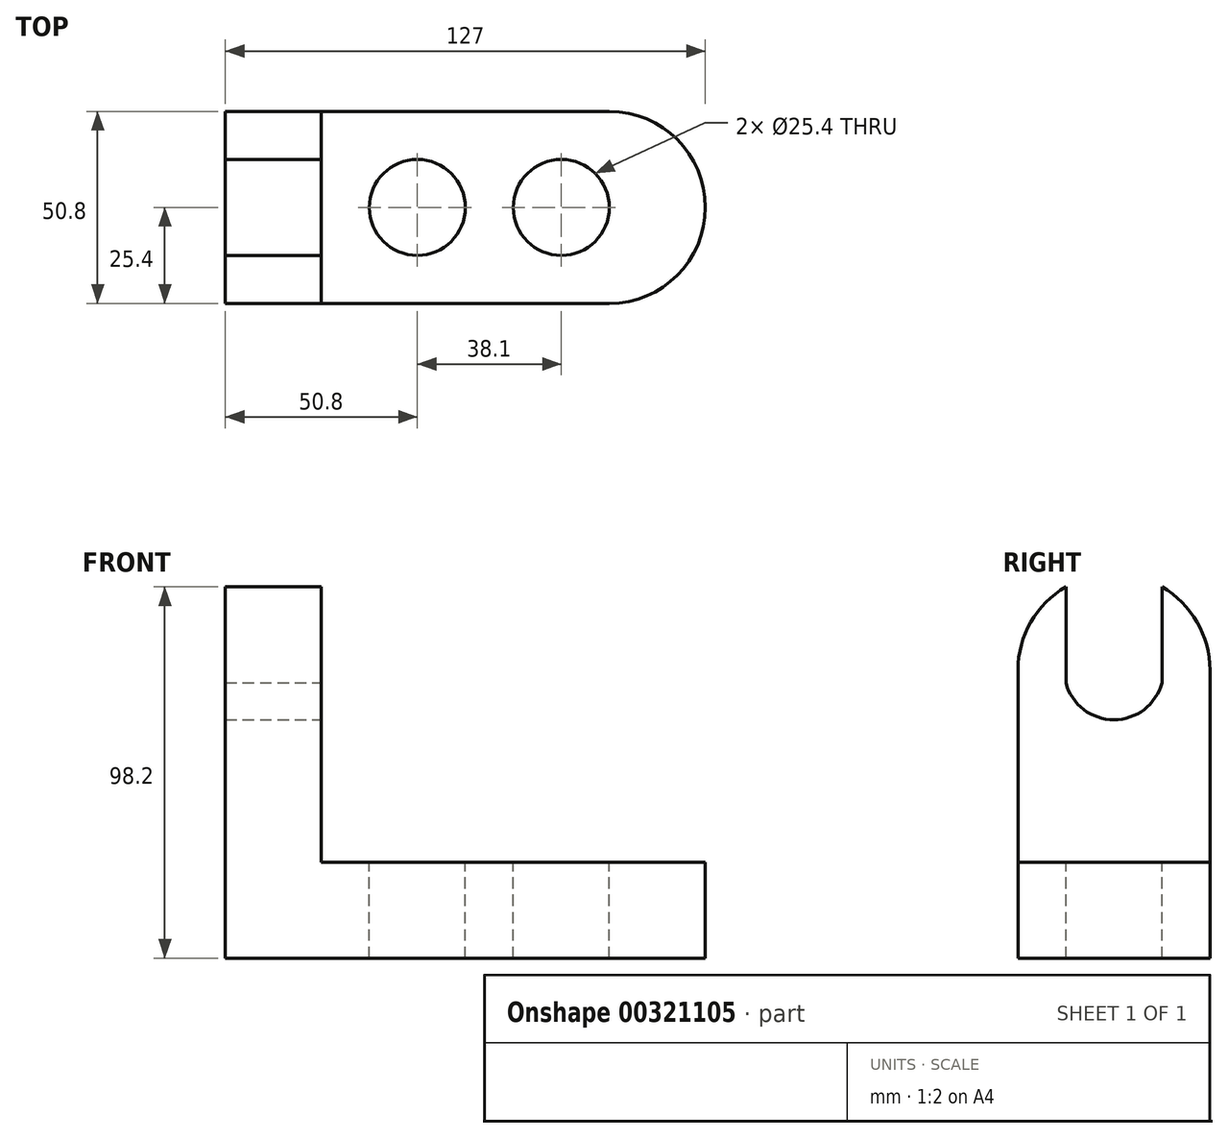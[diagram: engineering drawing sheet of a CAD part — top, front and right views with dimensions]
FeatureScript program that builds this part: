
annotation { "Feature Type Name" : "Feature", "Feature Type Description" : "" }
export const myFeature = defineFeature(function(context is Context, id is Id, definition is map)
    precondition{}
    {
        {
            var Q0;
            Q0=qCreatedBy(makeId("Top.planeOp"),FACE);
            var sketch = newSketch(context, id + "F0", { "sketchPlane" : qUnion([Q0])});
            skLineSegment(sketch, "E0", {"start": v(51.48, 35.05) * mm, "end": v(-50.12, 35.05) * mm});
            skLineSegment(sketch, "E1", {"start": v(-50.12, 35.05) * mm, "end": v(-50.12, -15.75) * mm});
            skLineSegment(sketch, "E2", {"start": v(-50.12, -15.75) * mm, "end": v(51.48, -15.75) * mm});
            skArc(sketch, "E3", {"start": v(51.48, -15.75) * mm, "mid": v(76.88, 9.65) * mm, "end": v(51.48, 35.05) * mm});
            skSolve(sketch);
        }
        {
            var Q0;
            Q0=makeQuery(id+"F0.imprint","IMPRINT",FACE,{"disambiguationData":[TD([[makeQuery(id+"F0.imprint","IMPRINT",EDGE,{"derivedFrom":sQuery(id+"F0.wireOp",EDGE,"E0")}),1.0]])]});
            extrude(context, id + "F1", {"entities" : qUnion([Q0]), "depth" : 25.4 * mm});
        }
        {
            var Q0;
            Q0=makeQuery(id+"F1.opExtrude","CAP_FACE",FACE,{"disambiguationData":[OSD([sQuery(id+"F0.wireOp",EDGE,"E0"),sQuery(id+"F0.wireOp",EDGE,"E1"),sQuery(id+"F0.wireOp",EDGE,"E2"),sQuery(id+"F0.wireOp",EDGE,"E3")])],"isStart":false});
            var sketch = newSketch(context, id + "F2", { "sketchPlane" : qUnion([Q0])});
            skPoint(sketch, "E4.endSnap0", {"position": v(-50.12, 9.65) * mm});
            skPoint(sketch, "E4.endSnap1", {"position": v(0.68, 35.05) * mm});
            skCircle(sketch, "E5", {"center": v(0.68, 9.65) * mm, "radius": 12.7 * mm});
            skSolve(sketch);
        }
        {
            var Q0;
            Q0=makeQuery(id+"F2.imprint","IMPRINT",FACE,{"disambiguationData":[TD([[makeQuery(id+"F2.imprint","IMPRINT",EDGE,{"derivedFrom":sQuery(id+"F2.wireOp",EDGE,"E5")}),1.0]])]});
            extrude(context, id + "F3", {"entities" : qUnion([Q0]), "operationType" : NewBodyOperationType.REMOVE, "oppositeDirection" : true, "depth" : 25.4 * mm});
        }
        {
            var Q0;
            Q0=makeQuery(id+"F1.opExtrude","CAP_FACE",FACE,{"disambiguationData":[OSD([sQuery(id+"F0.wireOp",EDGE,"E0"),sQuery(id+"F0.wireOp",EDGE,"E1"),sQuery(id+"F0.wireOp",EDGE,"E2"),sQuery(id+"F0.wireOp",EDGE,"E3")])],"isStart":false});
            var sketch = newSketch(context, id + "F4", { "sketchPlane" : qUnion([Q0])});
            skPoint(sketch, "E6.endSnap0", {"position": v(-50.12, 9.65) * mm});
            skCircle(sketch, "E7", {"center": v(38.78, 9.65) * mm, "radius": 12.7 * mm});
            skSolve(sketch);
        }
        {
            var Q0;
            Q0=makeQuery(id+"F4.imprint","IMPRINT",FACE,{"disambiguationData":[TD([[makeQuery(id+"F4.imprint","IMPRINT",EDGE,{"derivedFrom":sQuery(id+"F4.wireOp",EDGE,"E7")}),1.0]])]});
            extrude(context, id + "F5", {"entities" : qUnion([Q0]), "operationType" : NewBodyOperationType.REMOVE, "oppositeDirection" : true, "depth" : 25.4 * mm});
        }
        {
            var Q0;
            Q0=makeQuery(id+"F1.opExtrude","CAP_FACE",FACE,{"disambiguationData":[OSD([sQuery(id+"F0.wireOp",EDGE,"E0"),sQuery(id+"F0.wireOp",EDGE,"E1"),sQuery(id+"F0.wireOp",EDGE,"E2"),sQuery(id+"F0.wireOp",EDGE,"E3")])],"isStart":false});
            var sketch = newSketch(context, id + "F6", { "sketchPlane" : qUnion([Q0])});
            skLineSegment(sketch, "E8", {"start": v(-50.12, 35.05) * mm, "end": v(-50.12, -15.75) * mm});
            skLineSegment(sketch, "E9", {"start": v(-50.12, -15.75) * mm, "end": v(-24.72, -15.75) * mm});
            skLineSegment(sketch, "E10", {"start": v(-24.72, -15.75) * mm, "end": v(-24.72, 35.05) * mm});
            skLineSegment(sketch, "E11", {"start": v(-24.72, 35.05) * mm, "end": v(-50.12, 35.05) * mm});
            skSolve(sketch);
        }
        {
            var Q0;
            Q0=makeQuery(id+"F6.imprint","IMPRINT",FACE,{"disambiguationData":[TD([[makeQuery(id+"F6.imprint","IMPRINT",EDGE,{"derivedFrom":sQuery(id+"F6.wireOp",EDGE,"E8")}),1.0]])]});
            extrude(context, id + "F7", {"entities" : qUnion([Q0]), "operationType" : NewBodyOperationType.ADD, "depth" : 76.2 * mm});
        }
        {
            var Q0;
            Q0=makeQuery(id+"F7.opExtrude","SWEPT_FACE",FACE,{"disambiguationData":[OSD([sQuery(id+"F6.wireOp",EDGE,"E10")])]});
            var sketch = newSketch(context, id + "F8", { "sketchPlane" : qUnion([Q0])});
            skArc(sketch, "E12", {"start": v(35.05, 76.2) * mm, "mid": v(9.65, 101.6) * mm, "end": v(-15.75, 76.2) * mm});
            skPoint(sketch, "E12.centerSnap0", {"position": v(9.65, 25.4) * mm});
            skLineSegment(sketch, "E13", {"start": v(-15.75, 76.2) * mm, "end": v(-15.75, 101.6) * mm});
            skLineSegment(sketch, "E14", {"start": v(-15.75, 101.6) * mm, "end": v(35.05, 101.6) * mm});
            skLineSegment(sketch, "E15", {"start": v(35.05, 101.6) * mm, "end": v(35.05, 76.2) * mm});
            skSolve(sketch);
        }
        {
            var Q0;
            {var subQ0=sQuery(id+"F8.wireOp",EDGE,"E15");Q0=makeQuery(id+"F8.imprint","IMPRINT",FACE,{"disambiguationData":[TD([[makeQuery(id+"F8.imprint","IMPRINT",EDGE,{"derivedFrom":subQ0}),-1.0]])]});}
            extrude(context, id + "F9", {"entities" : qUnion([Q0]), "operationType" : NewBodyOperationType.REMOVE, "oppositeDirection" : true, "depth" : 25.4 * mm});
        }
        {
            var Q0;
            Q0=makeQuery(id+"F7.opExtrude","SWEPT_FACE",FACE,{"disambiguationData":[OSD([sQuery(id+"F6.wireOp",EDGE,"E10")])]});
            var sketch = newSketch(context, id + "F10", { "sketchPlane" : qUnion([Q0])});
            skLineSegment(sketch, "E16", {"start": v(9.65, 101.6) * mm, "end": v(-15.75, 101.6) * mm});
            skLineSegment(sketch, "E17", {"start": v(-15.75, 101.6) * mm, "end": v(-15.75, 76.2) * mm});
            skArc(sketch, "E18", {"start": v(35.05, 76.2) * mm, "mid": v(9.65, 101.6) * mm, "end": v(-15.75, 76.2) * mm});
            skSolve(sketch);
        }
        {
            var Q0;
            {var subQ0=sQuery(id+"F10.wireOp",EDGE,"E16");Q0=makeQuery(id+"F10.imprint","IMPRINT",FACE,{"disambiguationData":[TD([[makeQuery(id+"F10.imprint","IMPRINT",EDGE,{"derivedFrom":subQ0}),-1.0]])]});}
            extrude(context, id + "F11", {"entities" : qUnion([Q0]), "operationType" : NewBodyOperationType.REMOVE, "oppositeDirection" : true, "depth" : 25.4 * mm});
        }
        {
            var Q0;
            Q0=makeQuery(id+"F7.opExtrude","SWEPT_FACE",FACE,{"disambiguationData":[OSD([sQuery(id+"F6.wireOp",EDGE,"E10")])]});
            var sketch = newSketch(context, id + "F12", { "sketchPlane" : qUnion([Q0])});
            skPoint(sketch, "E19.startSnap0", {"position": v(9.65, 101.6) * mm});
            skLineSegment(sketch, "E20", {"start": v(-3.05, 98.2) * mm, "end": v(-3.05, 72.8) * mm});
            skLineSegment(sketch, "E21", {"start": v(22.35, 98.2) * mm, "end": v(22.35, 72.8) * mm});
            skArc(sketch, "E22", {"start": v(-3.05, 79.6) * mm, "mid": v(9.65, 63.05) * mm, "end": v(22.35, 79.6) * mm});
            skPoint(sketch, "E23.end.orphan", {"position": v(22.35, 101.6) * mm});
            skPoint(sketch, "E23.start.orphan", {"position": v(35.05, 101.6) * mm});
            skPoint(sketch, "E19.end.orphan", {"position": v(-3.05, 101.6) * mm});
            skPoint(sketch, "E19.start.orphan", {"position": v(-15.75, 101.6) * mm});
            skSolve(sketch);
        }
        {
            var Q0;
            {var subQ0=sQuery(id+"F12.wireOp",EDGE,"E22");var subQ7=sQuery(id+"F12.wireOp",EDGE,"E20");var subQ9=makeQuery(id+"F12.imprint","INTERSECT",VERTEX,{"disambiguationData":[OD(0.0)],"derivedFrom":[subQ7,subQ0]});Q0=makeQuery(id+"F12.imprint","IMPRINT",FACE,{"disambiguationData":[TD([[makeQuery(id+"F12.imprint","IMPRINT",EDGE,{"disambiguationData":[TD([[subQ9,1.0]])],"derivedFrom":subQ7}),1.0]])]});}
            extrude(context, id + "F13", {"entities" : qUnion([Q0]), "operationType" : NewBodyOperationType.REMOVE, "oppositeDirection" : true, "depth" : 25.4 * mm});
        }
    });
